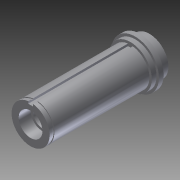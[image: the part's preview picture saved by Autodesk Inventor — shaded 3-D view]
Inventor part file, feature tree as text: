
AUTODESK INVENTOR PART (.ipt)
format: ipt  version: 2012 (Build 160160000, 160)  size: 158,720 bytes
history: native  units: in
note: dims shown in document units (in); Inventor stores cm internally (conversion verified against a paired STEP export)
features: extrude x8, sketch x6, plane x5
ambient origin geometry x8: Origin, YZ Plane, XZ Plane, XY Plane, X Axis, Y Axis, Z Axis, Center Point
feature tree (19):
  sketch  "Sketch1"  dims[d0=1.0in d4=0.5in]
  extrude  "Extrusion4"  Depth=0.5in
  plane  "Work Plane5"
  extrude  "Extrusion8"  [1 undecoded]
  plane  "Work Plane6"
  plane  "Work Plane9"
  plane  "Work Plane10"
  extrude  "Extrusion16"  Depth=0.045in TaperAngle=0.0deg
  extrude  "Extrusion17"  Depth=0.546in
  extrude  "Extrusion18"  Depth=0.125in
  plane  "Work Plane13"
  sketch  "Sketch16"  dims[d50=0.125in d51=0.125in]
  extrude  "Extrusion19"  Depth=0.5625in
  extrude  "Extrusion20"  Depth=0.045in TaperAngle=0.0deg
  extrude  "Extrusion21"  Depth=0.625in
  sketch  "Sketch6"  dims[d9=3.125in d10=0.0in d23=-0.125in]
  sketch  "Sketch14"  dims[d24=0.96in d25=0.045in d26=0.0in]
  sketch  "Sketch15"  dims[d27=-0.595in d36=-1.706in d39=0.546in]
  sketch  "Sketch17"  dims[d52=0.0625in d53=0.5625in d54=0.045in d55=0.0in d56=0.625in d57=0.3125in d58=0.0in d59=0.625in d60=0.3125in d61=0.0in d62=-0.25in d63=1.25in d64=0.125in d65=0.0in d66=0.25in d67=0.0in d68=1.125in d69=0.25in d70=0.0in]
note: 1 required parameter value undecoded (feature->parameter linkage not recoverable at this tier; creation-order binding heuristic only, values carry confidence <= 0.55)
